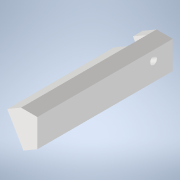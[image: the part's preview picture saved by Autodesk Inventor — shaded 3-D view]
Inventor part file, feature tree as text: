
AUTODESK INVENTOR PART (.ipt)
format: ipt  version: 2020 (Build 240168000, 168)  size: 180,736 bytes
history: native  units: mm
features: extrude x9, sketch x9, reference x5, projected_geometry x5, other x4, plane x2
ambient origin geometry x8: Origin, YZ Plane, XZ Plane, XY Plane, X Axis, Y Axis, Z Axis, Center Point
bodies: Volumenkörper1 (feature_tree)
feature tree (34):
  extrude  "Extrusion1"  Depth=3.0mm TaperAngle=0.0deg
  sketch  "Skizze2"  dims[d4=3.0mm d5=0.0mm d6=0.914mm d7=0.0mm]
  plane  "Arbeitsebene1"
  extrude  "Extrusion2"  Depth=3.0mm TaperAngle=0.0deg
  extrude  "Extrusion3"  Depth=6.0mm
  extrude  "Extrusion4"  Depth=2.4mm
  extrude  "Extrusion5"  Depth=2.0mm
  extrude  "Extrusion6"  Depth=30.0mm TaperAngle=0.0deg
  extrude  "Extrusion7"  Depth=2.0mm TaperAngle=0.0deg
  plane  "Arbeitsebene2"
  extrude  "Extrusion8"  [1 undecoded]
  extrude  "Extrusion9"  [1 undecoded]
  sketch  "Skizze1"  dims[d0=3.0mm d1=0.0mm d2=3.0mm d3=0.0mm]
  reference  "Referenz1"
  projected_geometry  "Projizierte Kontur1"
  reference  "Referenz2"
  sketch  "Skizze3"  dims[d8=30.0mm d9=0.0mm d10=6.0mm]
  reference  "Referenz3"
  projected_geometry  "Projizierte Kontur2"
  sketch  "Skizze4"  dims[d11=30.0mm d12=0.0mm d13=2.4mm]
  reference  "Referenz4"
  sketch  "Skizze6"  dims[d14=25.0mm d15=2.0mm]
  projected_geometry  "Projizierte Kontur3"
  sketch  "Skizze7"  dims[d16=5.0mm d17=30.0mm d18=0.0mm]
  projected_geometry  "Projizierte Kontur4"
  sketch  "Skizze8"  dims[d19=4.4mm d20=2.0mm d21=0.0mm]
  sketch  "Skizze9"  dims[d22=6.5mm d23=0.5mm d24=0.0mm d25=0.0mm]
  reference  "Referenz5"
  sketch  "Skizze10"
  projected_geometry  "Projizierte Kontur5"
  parser-record x1  (decoder bookkeeping rows leaked as tree rows — omitted from the tree; the rows remain in map.json)
  other  "GlassesAssembly.iam"
  other  "CameraArm:1"
  other  "BallJoint:1"
note: 2 required parameter values undecoded (feature->parameter linkage not recoverable at this tier; creation-order binding heuristic only, values carry confidence <= 0.55)
note: 1 file-system path scrubbed to <path> (originals preserved in map.json)
